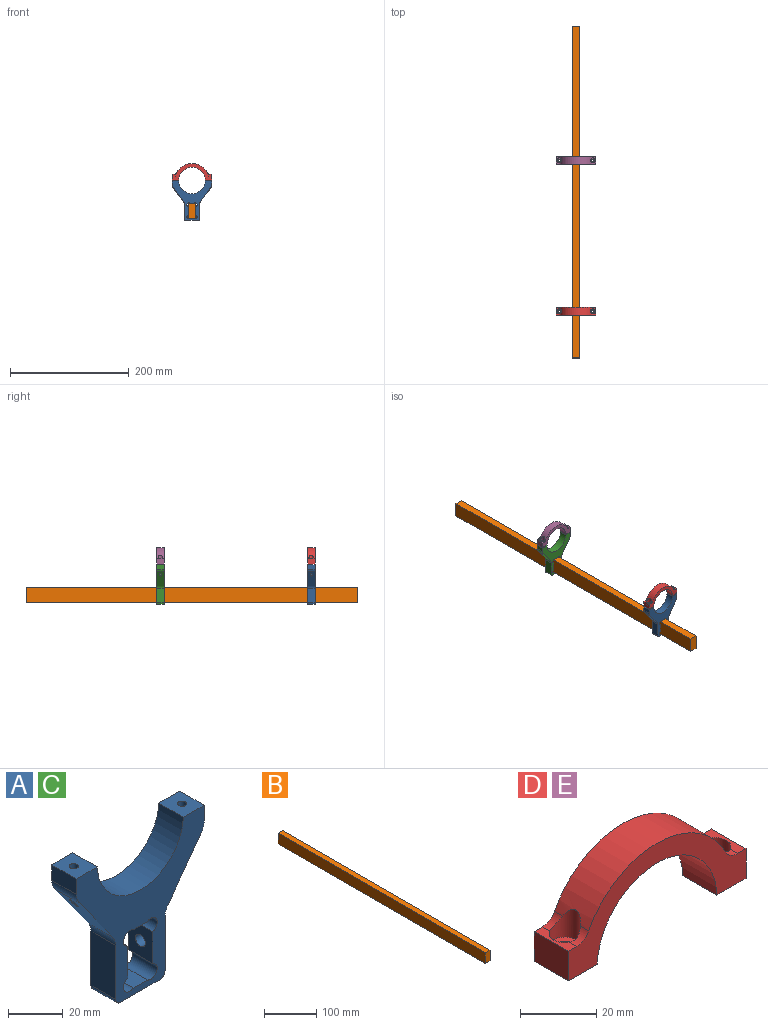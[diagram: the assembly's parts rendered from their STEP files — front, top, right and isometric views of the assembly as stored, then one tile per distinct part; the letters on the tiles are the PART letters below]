
ASSEMBLY  parts=5 mates=4
PART A: 29 faces, bbox 67x13.7x67.5 mm
  f0: plane 12.7x10.81mm, normal (0,0,1), area 128.7mm2, adj f1,f13,f14,f15,f17
  f1: plane 12.7x6.93mm, normal (-1,0,0), area 88mm2, adj f0,f14,f15,f27
  f2: plane 24.9x18.31mm, normal (-0.81,0,-0.59), area 360.9mm2, adj f14,f15,f17,f25,f27
  f3: plane 24.2x12.7mm, normal (-1,0,0), area 307.3mm2, adj f14,f15,f23,f25
  f4: plane 20.45x12.7mm, normal (0,0,-1), area 259.7mm2, adj f14,f15,f23,f24
  f5: plane 24.2x12.7mm, normal (1,0,0), area 286.8mm2, adj f14,f15,f16,f24,f26
  f6: plane 23.94x17.36mm, normal (0.81,0,-0.59), area 360.9mm2, adj f14,f15,f18,f26,f28
  f7: plane 12.7x6.93mm, normal (1,0,0), area 88mm2, adj f8,f14,f15,f28
  f8: plane 12.7x10.81mm, normal (0,0,1), area 128.7mm2, adj f7,f13,f14,f15,f18
  f9: plane 12.7x7.28mm, normal (0,0,1), area 92.4mm2, adj f14,f15,f20,f22
  f10: plane 14.29x12.7mm, normal (1,0,0), area 181.5mm2, adj f14,f15,f19,f22
  f11: plane 12.7x7.28mm, normal (0,0,-1), area 92.4mm2, adj f14,f15,f19,f21
  f12: plane 14.29x12.7mm, normal (-1,0,0), area 161mm2, adj f14,f15,f16,f20,f21
  f13: cylinder r=22.23mm len=44.42mm, axis (0,1,0), area 867.4mm2, adj f0,f8,f14,f15
  f14: plane 66.55x66.04mm, normal (0,-1,0), area 1518.7mm2, adj f0,f1,f2,f3,f4,f5,f6,f7
  f15: plane 66.55x66.04mm, normal (0,1,0), area 1518.7mm2, adj f0,f1,f2,f3,f4,f5,f6,f7
  f16: cylinder r=2.55mm len=6.35mm, axis (-1,0,0), area 101.8mm2, adj f5,f12
  f17: cylinder r=1.65mm len=18.68mm, axis (0,0,1), area 170.1mm2, adj f0,f2
  f18: cylinder r=1.65mm len=18.71mm, axis (0,0,1), area 170.1mm2, adj f6,f8
  f19: cylinder r=3.3mm len=12.7mm, axis (0,-1,0), area 142.2mm2, adj f10,f11,f14,f15
  f20: cylinder r=3.3mm len=12.7mm, axis (0,-1,0), area 142.2mm2, adj f9,f12,f14,f15
  f21: cylinder r=3.3mm len=12.7mm, axis (0,-1,0), area 142.2mm2, adj f11,f12,f14,f15
  f22: cylinder r=3.3mm len=12.7mm, axis (0,-1,0), area 142.2mm2, adj f9,f10,f14,f15
  f23: cylinder r=2.54mm len=12.7mm, axis (0,1,0), area 50.7mm2, adj f3,f4,f14,f15
  f24: cylinder r=2.54mm len=12.7mm, axis (0,1,0), area 50.7mm2, adj f4,f5,f14,f15
  f25: cylinder r=7.62mm len=12.7mm, axis (0,-1,0), area 60.7mm2, adj f2,f3,f14,f15
  f26: cylinder r=7.62mm len=12.7mm, axis (0,1,0), area 60.7mm2, adj f5,f6,f14,f15
  f27: cylinder r=7.62mm len=12.7mm, axis (0,1,0), area 60.7mm2, adj f1,f2,f14,f15
  f28: cylinder r=7.62mm len=12.7mm, axis (0,1,0), area 60.7mm2, adj f6,f7,f14,f15
PART B: 6 faces, bbox 12.7x558.8x25.4 mm
  f0: plane 558.8x25.4mm, normal (1,0,0), area 14193.5mm2, adj f1,f3,f4,f5
  f1: plane 558.8x12.7mm, normal (0,0,1), area 7096.8mm2, adj f0,f2,f4,f5
  f2: plane 558.8x25.4mm, normal (-1,0,0), area 14193.5mm2, adj f1,f3,f4,f5
  f3: plane 558.8x12.7mm, normal (0,0,-1), area 7096.8mm2, adj f0,f2,f4,f5
  f4: plane 25.4x12.7mm, normal (0,-1,0), area 322.6mm2, adj f0,f1,f2,f3
  f5: plane 25.4x12.7mm, normal (0,1,0), area 322.6mm2, adj f0,f1,f2,f3
PART C: same geometry as A
PART D: 20 faces, bbox 66x12.7x27.8 mm
  f0: cylinder r=5.08mm len=4.52mm, axis (0,1,0), area 13.9mm2, adj f1,f6,f12,f19
  f1: cylinder r=28.57mm len=50.84mm, axis (0,1,0), area 766.4mm2, adj f0,f2,f3,f11,f12,f13,f16,f19
  f2: cylinder r=5.08mm len=4.52mm, axis (0,1,0), area 13.9mm2, adj f1,f4,f11,f16
  f3: cylinder r=5.08mm len=4.52mm, axis (0,1,0), area 13.9mm2, adj f1,f4,f12,f16
  f4: plane 12.7x3.08mm, normal (0,0,1), area 28.2mm2, adj f2,f3,f7,f11,f12,f16
  f5: plane 12.7x9.53mm, normal (1,0,0), area 121mm2, adj f6,f10,f11,f12
  f6: plane 12.7x3.08mm, normal (0,0,1), area 28.2mm2, adj f0,f5,f11,f12,f13,f19
  f7: plane 12.7x9.53mm, normal (-1,0,0), area 121mm2, adj f4,f8,f11,f12
  f8: plane 12.7x10.81mm, normal (0,0,-1), area 122.1mm2, adj f7,f9,f11,f12,f14
  f9: cylinder r=22.23mm len=44.42mm, axis (0,1,0), area 867.4mm2, adj f8,f10,f11,f12
  f10: plane 12.7x10.81mm, normal (0,0,-1), area 122.1mm2, adj f5,f9,f11,f12,f17
  f11: plane 66.04x27.81mm, normal (0,-1,0), area 598.2mm2, adj f1,f2,f4,f5,f6,f7,f8,f9
  f12: plane 66.04x27.81mm, normal (0,1,0), area 598.2mm2, adj f0,f1,f3,f4,f5,f6,f7,f8
  f13: cylinder r=5.08mm len=4.52mm, axis (0,1,0), area 13.9mm2, adj f1,f6,f11,f19
  f14: cylinder r=2.2mm len=5.53mm, axis (0,0,1), area 76.4mm2, adj f8,f15
  f15: plane 8.25x8.25mm, normal (0,0,1), area 38.3mm2, adj f14,f16
  f16: cylinder r=4.12mm len=9.5mm, axis (0,0,1), area 146.3mm2, adj f1,f2,f3,f4,f15
  f17: cylinder r=2.2mm len=5.53mm, axis (0,0,1), area 76.4mm2, adj f10,f18
  f18: plane 8.25x8.25mm, normal (0,0,1), area 38.3mm2, adj f17,f19
  f19: cylinder r=4.12mm len=9.51mm, axis (0,0,1), area 146.3mm2, adj f0,f1,f6,f13,f18
PART E: same geometry as D
PLACE A t=(0.05,-215.19,12.8)mm
PLACE B t=(-0.01,-14.32,0.1)mm fixed
PLACE C t=(0.05,38.81,12.8)mm
PLACE D t=(0.05,-215.19,50.9)mm
PLACE E t=(0.05,38.81,50.9)mm
MATE revolute D.f1 <-> A.f13  axis (0,1,0) through (0.05,-215.19,50.9)mm
MATE planar D.f11 <-> A.f14  axis (0,-1,0) through (0.05,-221.54,65.68)mm
MATE planar A.f16 <-> B.f2  axis (1,0,0) through (-6.36,-215.19,-0.28)mm
MATE planar A.f11 <-> B.f1  axis (0,0,-1) through (0.05,-215.19,12.8)mm
